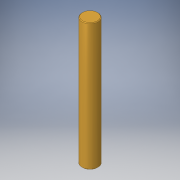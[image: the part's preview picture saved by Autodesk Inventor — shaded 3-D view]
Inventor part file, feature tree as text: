
AUTODESK INVENTOR PART (.ipt)
format: ipt  version: 2016 (Build 200138000, 138)  size: 92,160 bytes
history: native  units: in
note: dims shown in document units (in); Inventor stores cm internally (conversion verified against a paired STEP export)
features: extrude x1, chamfer x1, sketch x1
ambient origin geometry x8: Origin, YZ Plane, XZ Plane, XY Plane, X Axis, Y Axis, Z Axis, Center Point
bodies: Solid1 (feature_tree)
feature tree (3):
  extrude  "Extrusion1"  Depth=2.0in TaperAngle=0.0deg
  chamfer  "Chamfer1"  Distance=0.125in Angle=45.0deg
  sketch  "Sketch1"  dims[d0=0.25in d1=2.0in d2=0.0in d3=0.01in d4=0.125in d5=45.0deg]
